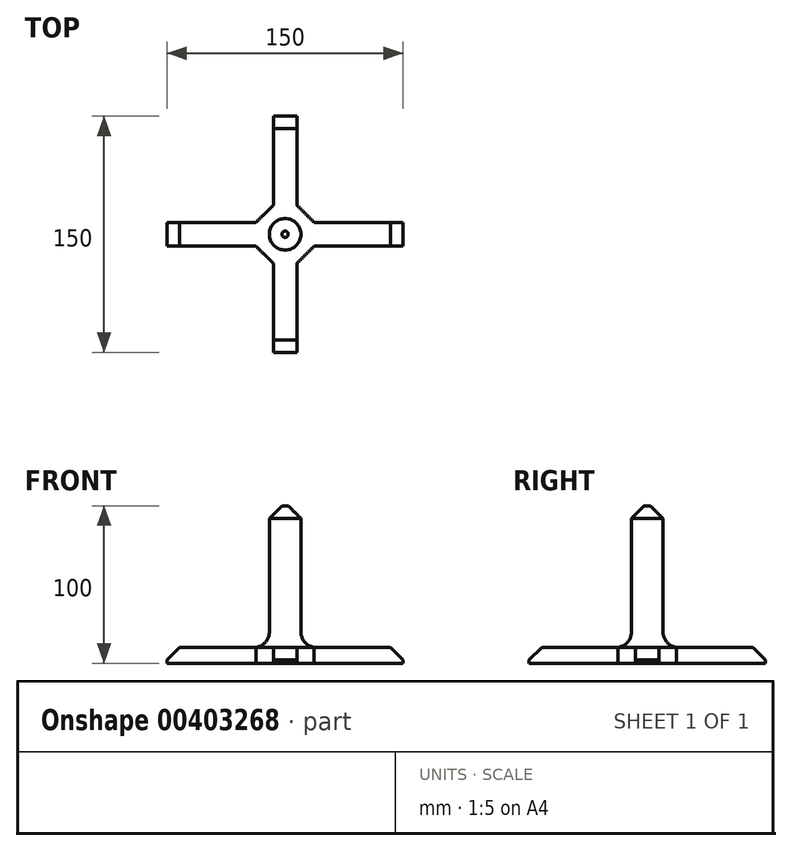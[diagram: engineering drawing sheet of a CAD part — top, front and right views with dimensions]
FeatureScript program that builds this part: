
annotation { "Feature Type Name" : "Feature", "Feature Type Description" : "" }
export const myFeature = defineFeature(function(context is Context, id is Id, definition is map)
    precondition{}
    {
        {
            var Q0;
            Q0=qCreatedBy(makeId("Top.planeOp"),FACE);
            var sketch = newSketch(context, id + "F0", { "sketchPlane" : qUnion([Q0])});
            skLineSegment(sketch, "E0.bottom", {"start": v(-75, 7.5) * mm, "end": v(75, 7.5) * mm});
            skLineSegment(sketch, "E0.top", {"start": v(-75, -7.5) * mm, "end": v(75, -7.5) * mm});
            skLineSegment(sketch, "E0.left", {"start": v(-75, 7.5) * mm, "end": v(-75, -7.5) * mm});
            skLineSegment(sketch, "E0.right", {"start": v(75, 7.5) * mm, "end": v(75, -7.5) * mm});
            skLineSegment(sketch, "E1.bottom", {"start": v(-7.5, 75) * mm, "end": v(7.5, 75) * mm});
            skLineSegment(sketch, "E1.top", {"start": v(-7.5, -75) * mm, "end": v(7.5, -75) * mm});
            skLineSegment(sketch, "E1.left", {"start": v(-7.5, 75) * mm, "end": v(-7.5, -75) * mm});
            skLineSegment(sketch, "E1.right", {"start": v(7.5, 75) * mm, "end": v(7.5, -75) * mm});
            skSolve(sketch);
        }
        {
            var Q0;
            Q0 = qSketchRegion(id + "F0", true);
            extrude(context, id + "F1", {"entities" : qUnion([Q0]), "depth" : 10 * mm});
        }
        {
            var Q0;
            Q0=qCreatedBy(makeId("Top.planeOp"),FACE);
            var sketch = newSketch(context, id + "F2", { "sketchPlane" : qUnion([Q0])});
            skCircle(sketch, "E2", {"center": v(0, 0) * mm, "radius": 10 * mm});
            skSolve(sketch);
        }
        {
            var Q0;
            Q0 = qSketchRegion(id + "F2", true);
            extrude(context, id + "F3", {"entities" : qUnion([Q0]), "operationType" : NewBodyOperationType.ADD, "depth" : 100 * mm});
        }
        {
            var Q0;
            Q0=makeQuery(id+"F3.boolean.opBoolean","INTERSECT",EDGE,{"derivedFrom":[makeQuery(id+"F1.opExtrude","CAP_FACE",FACE,{"disambiguationData":[OSD([sQuery(id+"F0.wireOp",EDGE,"E0.bottom"),sQuery(id+"F0.wireOp",EDGE,"E0.top"),sQuery(id+"F0.wireOp",EDGE,"E0.left"),sQuery(id+"F0.wireOp",EDGE,"E0.right"),sQuery(id+"F0.wireOp",EDGE,"E1.bottom"),sQuery(id+"F0.wireOp",EDGE,"E1.top"),sQuery(id+"F0.wireOp",EDGE,"E1.left"),sQuery(id+"F0.wireOp",EDGE,"E1.right")])],"isStart":false}),makeQuery(id+"F3.opExtrude","SWEPT_FACE",FACE,{"disambiguationData":[OSD([sQuery(id+"F2.wireOp",EDGE,"E2")])]})]});
            fillet(context, id + "F4", {"entities" : qUnion([Q0]), "radius" : 10 * mm, "tangentPropagation" : true, "allowEdgeOverflow" : false});
        }
        {
            var Q0;
            Q0=makeQuery(id+"F1.opExtrude","SWEPT_EDGE",EDGE,{"disambiguationData":[OSD([sQuery(id+"F0.wireOp",EDGE,"E0.top"),sQuery(id+"F0.wireOp",EDGE,"E1.left")])]});
            var Q1;
            Q1=makeQuery(id+"F1.opExtrude","SWEPT_EDGE",EDGE,{"disambiguationData":[OSD([sQuery(id+"F0.wireOp",EDGE,"E0.top"),sQuery(id+"F0.wireOp",EDGE,"E1.right")])]});
            var Q2;
            Q2=makeQuery(id+"F1.opExtrude","SWEPT_EDGE",EDGE,{"disambiguationData":[OSD([sQuery(id+"F0.wireOp",EDGE,"E0.bottom"),sQuery(id+"F0.wireOp",EDGE,"E1.right")])]});
            var Q3;
            Q3=makeQuery(id+"F1.opExtrude","SWEPT_EDGE",EDGE,{"disambiguationData":[OSD([sQuery(id+"F0.wireOp",EDGE,"E0.bottom"),sQuery(id+"F0.wireOp",EDGE,"E1.left")])]});
            chamfer(context, id + "F5", {"entities" : qUnion([Q0, Q1, Q2, Q3]), "width" : 11 * mm, "tangentPropagation" : true});
        }
        {
            var Q0;
            Q0=makeQuery(id+"F1.opExtrude","CAP_EDGE",EDGE,{"disambiguationData":[OSD([sQuery(id+"F0.wireOp",EDGE,"E0.left")])],"isStart":false});
            var Q1;
            Q1=makeQuery(id+"F1.opExtrude","CAP_EDGE",EDGE,{"disambiguationData":[OSD([sQuery(id+"F0.wireOp",EDGE,"E1.top")])],"isStart":false});
            var Q2;
            Q2=makeQuery(id+"F1.opExtrude","CAP_EDGE",EDGE,{"disambiguationData":[OSD([sQuery(id+"F0.wireOp",EDGE,"E0.right")])],"isStart":false});
            var Q3;
            Q3=makeQuery(id+"F1.opExtrude","CAP_EDGE",EDGE,{"disambiguationData":[OSD([sQuery(id+"F0.wireOp",EDGE,"E1.bottom")])],"isStart":false});
            var Q4;
            Q4=makeQuery(id+"F3.opExtrude","CAP_EDGE",EDGE,{"disambiguationData":[OSD([sQuery(id+"F2.wireOp",EDGE,"E2")])],"isStart":false});
            chamfer(context, id + "F6", {"entities" : qUnion([Q0, Q1, Q2, Q3, Q4]), "width" : 8 * mm, "tangentPropagation" : true});
        }
    });
